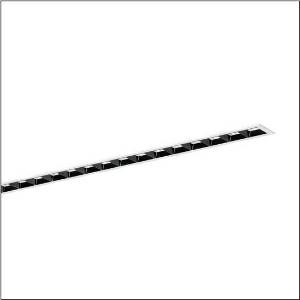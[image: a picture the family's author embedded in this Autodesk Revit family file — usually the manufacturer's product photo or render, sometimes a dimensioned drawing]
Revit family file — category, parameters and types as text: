
# Revit family: silica_r__21_51mx14dc4awb_d642
name_source: partatom
category: Lighting Fixtures
units: mm (PartAtom-declared; Revit-internal decimal feet)

## family parameters
Cut with Voids When Loaded = No
Host = Face
Light Source = No
Part Type = Normal
Room Calculation Point = No
Round Connector Dimension = Use Diameter
Shared = No

## types (1)
- --- (1 x LED, 10800 lm, 73.7 W, 4000K)
    Apparent Load = 74 VA
    CIE Flux Codes = 74 94 99 100 100
    Color Rendering = 80
    Color Temperature = 4000K
    Default Elevation = 1800 mm
    Description = Silica® 21, office luminaire, primary light control with darklight reflector, of PMMA, black, light emission: direct distribution, primary light characteristic: asymmetric, installation type: recessed, LED, rated luminous flux: 10.800lm, luminous efficacy: 147lm/W, light colour: 840, colour temperature: 4000K, control gear: DALI 2, with terminal, 3+2-pole, max. 2.5mm², mains connection: 220..240V, AC, 50/60Hz, rated input power: 73.7W, luminaire housing, of aluminium, traffic white (RAL 9016), length: 3.028mm, width: 79mm, height: 53mm, protection rating (complete): IP20, insulation class (complete): insulation class I (protective earthing), certification: CE, ENEC, VDE, permissible operating ambient temperature: 0..+35°C, standard: EN 50419, packaging unit: 1 piece
    Height = 0 mm  [stored 0 ft]
    Lamp = 1 x LED
    Lamp Light Flux = 10800 lm
    Lamp Power = 73.7 W
    Lamp count = 1
    Length = 3027 mm
    Luminous efficacy = 147 lm/W
    Manufacturer = Siteco
    ModVariant = No
    Model = 51MX14DC4AWB
    Mounting Place = Ceiling
    Mounting Type = Recessed
    Number of Poles = 1
    OnlyDefault = Yes
    Power Factor = 1
    Product Name = Silica® 21
    Product group = office luminaire | ceiling recessed
    ProductGroupID = 401
    Protection Class = Protection class I
    Protection Degree = IP 20
    RLX_Detail_Level = 1
    RLX_Emergency_Light_Flux = 0 lm
    RLX_Emergency_Type = 0
    RLX_Emergency_Type_DB = No
    RlxData = <blob elided: 63485 chars, md5=a6e7e3ea>
    Socket = socket
    Standby Power = 0 W
    System Light Flux = 10800 lm
    System Power = 74 W
    Type Comments = factory setting: luminous flux: 100 % | dim-lin: 254 | 418 mA
    Type Image = l_1335880.jpg
    URL = http://relux.com
    VarID = @adj_122362
    Voltage = 0 V
    Weight = 0.00 kg
    Width = 79 mm

note: [stored X ft] marks values corroborated as IEEE doubles in the binary element streams (Revit-internal decimal feet)

## geometry (parser evidence)
native form markers: Blend x4, Sweep x9
no freeform markers — native parametric forms only
